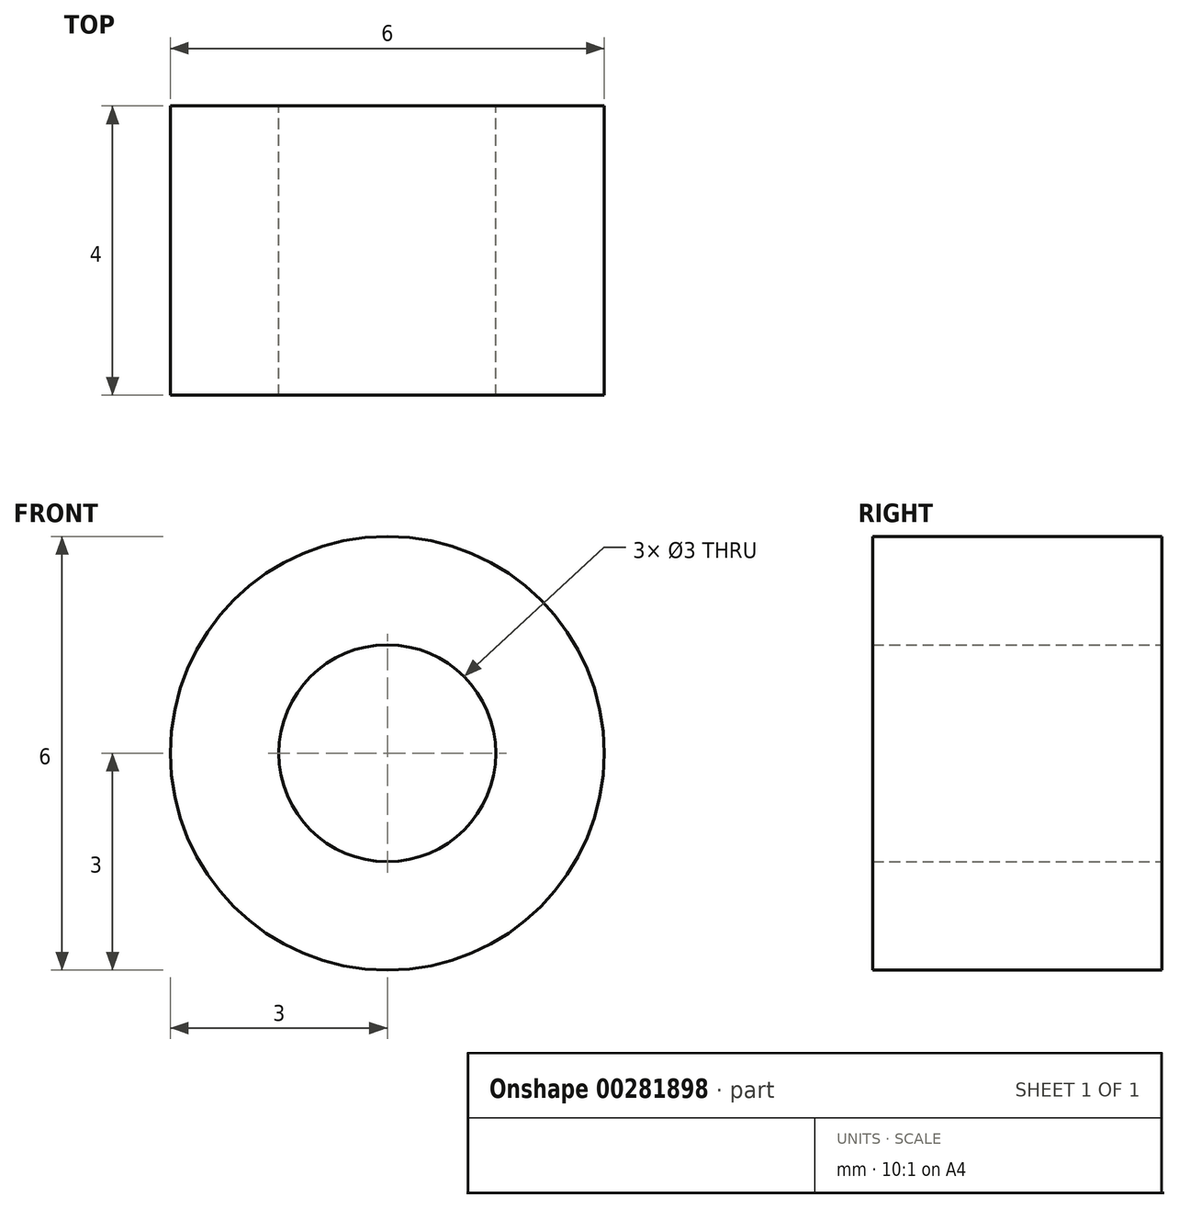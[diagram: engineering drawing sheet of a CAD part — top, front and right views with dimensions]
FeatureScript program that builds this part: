
annotation { "Feature Type Name" : "Feature", "Feature Type Description" : "" }
export const myFeature = defineFeature(function(context is Context, id is Id, definition is map)
    precondition{}
    {
        {
            var Q0;
            Q0=qCreatedBy(makeId("Front.planeOp"),FACE);
            var sketch = newSketch(context, id + "F0", { "sketchPlane" : qUnion([Q0])});
            skCircle(sketch, "E0", {"center": v(0, 0) * mm, "radius": 1.5 * mm});
            skCircle(sketch, "E1", {"center": v(0, 0) * mm, "radius": 3 * mm});
            skSolve(sketch);
        }
        {
            var Q0;
            Q0=qSketchRegion(id+"F0",true);
            extrude(context, id + "F1", {"entities" : qUnion([Q0]), "depth" : 4 * mm});
        }
    });
